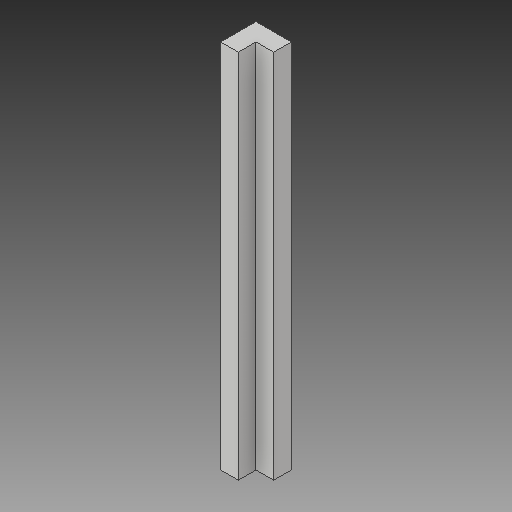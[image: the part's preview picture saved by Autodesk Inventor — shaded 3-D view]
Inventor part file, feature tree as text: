
AUTODESK INVENTOR PART (.ipt)
format: ipt  version: 2017 (Build 210142000, 142)  size: 84,480 bytes
history: native  units: in
note: dims shown in document units (in); Inventor stores cm internally (conversion verified against a paired STEP export)
features: other x3, sketch x3
ambient origin geometry x8: Origin, YZ Plane, XZ Plane, XY Plane, X Axis, Y Axis, Z Axis, Center Point
bodies: Solid1 (feature_tree)
feature tree (6):
  other  "rev1 corners.ipt"
  other  "Solid1::rev1 corners.ipt"
  other  "TaggingFeature1"
  sketch  "Sketch1"  dims[d0=0.3937in]
  sketch  "Sketch2"
  sketch  "Sketch3"
